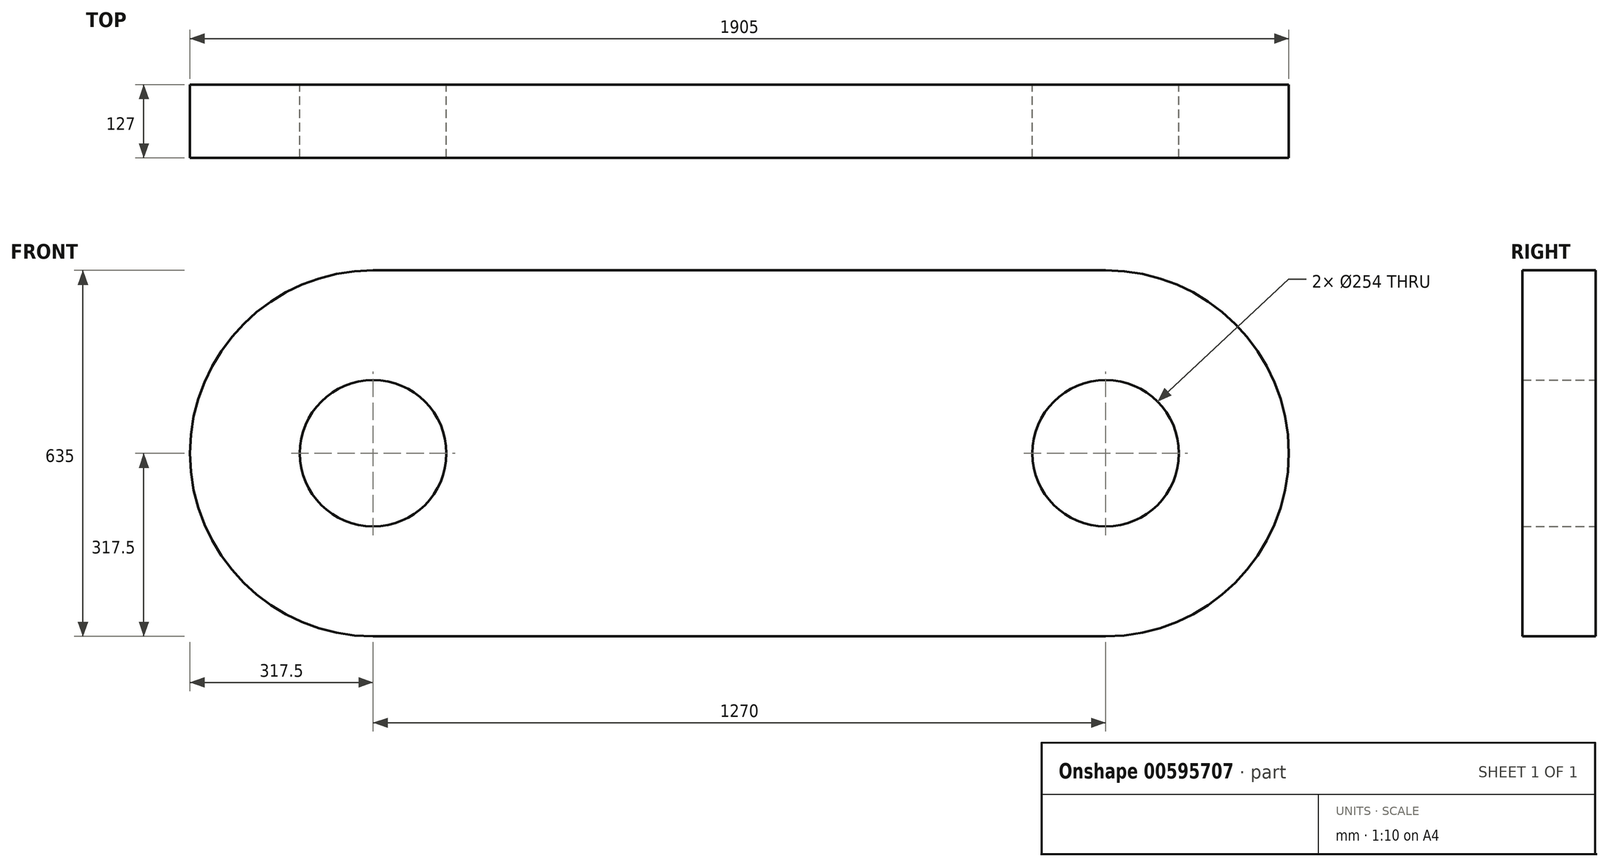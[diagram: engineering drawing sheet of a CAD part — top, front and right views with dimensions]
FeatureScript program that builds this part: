
annotation { "Feature Type Name" : "Feature", "Feature Type Description" : "" }
export const myFeature = defineFeature(function(context is Context, id is Id, definition is map)
    precondition{}
    {
        {
            var Q0;
            Q0=qCreatedBy(makeId("Front.planeOp"),FACE);
            var sketch = newSketch(context, id + "F0", { "sketchPlane" : qUnion([Q0])});
            skLineSegment(sketch, "E0.bottom", {"start": v(-635, 317.5) * mm, "end": v(635, 317.5) * mm});
            skLineSegment(sketch, "E0.top", {"start": v(-635, -317.5) * mm, "end": v(635, -317.5) * mm});
            skArc(sketch, "E1", {"start": v(-635, 317.5) * mm, "mid": v(-952.5, 0) * mm, "end": v(-635, -317.5) * mm});
            skArc(sketch, "E2", {"start": v(635, -317.5) * mm, "mid": v(952.5, 0) * mm, "end": v(635, 317.5) * mm});
            skCircle(sketch, "E3", {"center": v(635, 0) * mm, "radius": 127 * mm});
            skCircle(sketch, "E4", {"center": v(-635, 0) * mm, "radius": 127 * mm});
            skSolve(sketch);
        }
        {
            var Q0;
            Q0=makeQuery(id+"F0.imprint","IMPRINT",FACE,{"disambiguationData":[TD([[makeQuery(id+"F0.imprint","IMPRINT",EDGE,{"derivedFrom":sQuery(id+"F0.wireOp",EDGE,"E0.bottom")}),-1.0]])]});
            extrude(context, id + "F1", {"entities" : qUnion([Q0]), "endBound" : BoundingType.SYMMETRIC, "depth" : 127 * mm, "offsetDistance" : 25.4 * mm});
        }
    });
